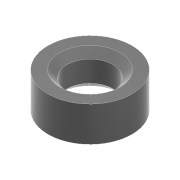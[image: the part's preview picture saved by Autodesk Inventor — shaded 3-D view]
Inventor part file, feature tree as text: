
AUTODESK INVENTOR PART (.ipt)
format: ipt  version: 2022 (Build 260153000, 153)  size: 98,816 bytes
history: native  units: mm
features: sketch x2, extrude x1, hole x1, chamfer x1
ambient origin geometry x8: Origin, YZ Plane, XZ Plane, XY Plane, X Axis, Y Axis, Z Axis, Center Point
bodies: Solid1 (feature_tree)
feature tree (5):
  extrude  "Extrusion1"  Depth=2.5mm TaperAngle=0.0deg
  hole  "Hole1"  [1 undecoded]
  chamfer  "Chamfer1"  [1 undecoded]
  sketch  "Sketch1"  dims[d0=6.0mm d1=2.5mm d2=0.0mm]
  sketch  "Sketch2"  dims[d3=3.3mm d4=6.0mm d5=4.0mm d6=2.0mm d7=90.0deg d8=8.0mm d9=20.594885mm d10=0.5mm d11=2.0mm d12=45.0deg]
note: 2 required parameter values undecoded (feature->parameter linkage not recoverable at this tier; creation-order binding heuristic only, values carry confidence <= 0.55)
